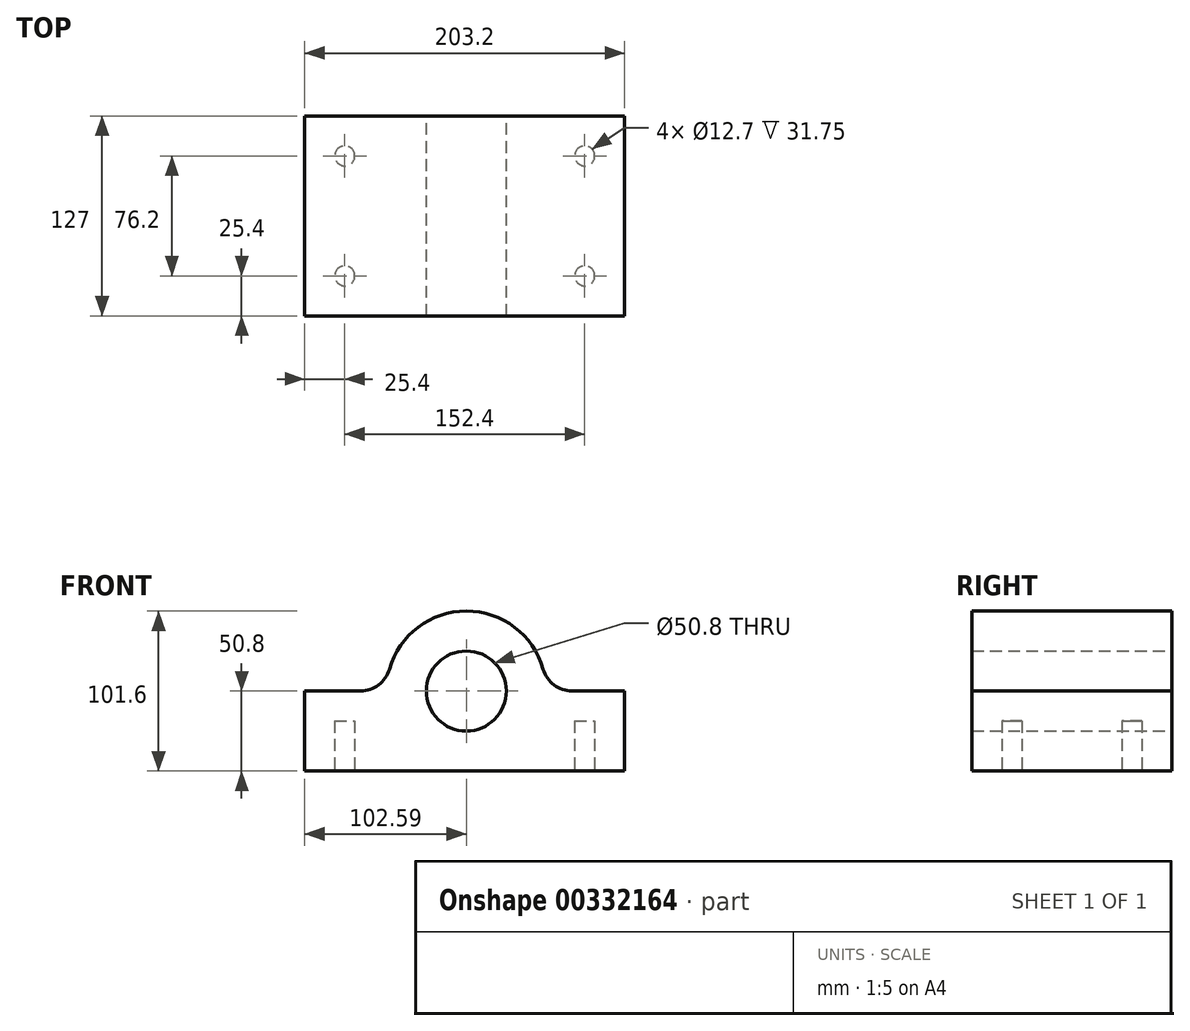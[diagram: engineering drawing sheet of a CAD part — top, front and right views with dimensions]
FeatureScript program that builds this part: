
annotation { "Feature Type Name" : "Feature", "Feature Type Description" : "" }
export const myFeature = defineFeature(function(context is Context, id is Id, definition is map)
    precondition{}
    {
        {
            var Q0;
            Q0=qCreatedBy(makeId("Front.planeOp"),FACE);
            var sketch = newSketch(context, id + "F0", { "sketchPlane" : qUnion([Q0])});
            skCircle(sketch, "E0", {"center": v(0, 0) * mm, "radius": 25.4 * mm});
            skLineSegment(sketch, "E1", {"start": v(100.6, 0) * mm, "end": v(100.6, -50.8) * mm});
            skLineSegment(sketch, "E2", {"start": v(100.6, -50.8) * mm, "end": v(-102.6, -50.8) * mm});
            skLineSegment(sketch, "E3", {"start": v(-102.6, -50.8) * mm, "end": v(-102.6, 0) * mm});
            skArc(sketch, "E4", {"start": v(48.87, 13.85) * mm, "mid": v(0, 50.8) * mm, "end": v(-48.87, 13.85) * mm});
            skLineSegment(sketch, "E5", {"start": v(-102.6, 0) * mm, "end": v(-67.2, 0) * mm});
            skLineSegment(sketch, "E6", {"start": v(100.6, 0) * mm, "end": v(67.2, 0) * mm});
            skArc(sketch, "E7", {"start": v(-67.2, 0) * mm, "mid": v(-55.71, 3.85) * mm, "end": v(-48.87, 13.85) * mm});
            skArc(sketch, "E8", {"start": v(48.87, 13.85) * mm, "mid": v(55.71, 3.85) * mm, "end": v(67.2, 0) * mm});
            skSolve(sketch);
        }
        {
            var Q0;
            Q0=makeQuery(id+"F0.imprint","IMPRINT",FACE,{"disambiguationData":[TD([[makeQuery(id+"F0.imprint","IMPRINT",EDGE,{"derivedFrom":sQuery(id+"F0.wireOp",EDGE,"E0")}),-1.0]])]});
            extrude(context, id + "F1", {"entities" : qUnion([Q0]), "depth" : 127 * mm});
        }
        {
            var Q0;
            Q0=makeQuery(id+"F1.opExtrude","SWEPT_FACE",FACE,{"disambiguationData":[OSD([sQuery(id+"F0.wireOp",EDGE,"E2")])]});
            var sketch = newSketch(context, id + "F2", { "sketchPlane" : qUnion([Q0])});
            skCircle(sketch, "E9", {"center": v(75.2, 101.6) * mm, "radius": 6.35 * mm});
            skCircle(sketch, "E10", {"center": v(75.2, 25.4) * mm, "radius": 6.35 * mm});
            skCircle(sketch, "E11", {"center": v(-77.2, 101.6) * mm, "radius": 6.35 * mm});
            skCircle(sketch, "E12", {"center": v(-77.2, 25.4) * mm, "radius": 6.35 * mm});
            skSolve(sketch);
        }
        {
            var Q0;
            Q0=makeQuery(id+"F2.imprint","IMPRINT",FACE,{"disambiguationData":[TD([[makeQuery(id+"F2.imprint","IMPRINT",EDGE,{"derivedFrom":sQuery(id+"F2.wireOp",EDGE,"E11")}),1.0]])]});
            var Q1;
            Q1=makeQuery(id+"F2.imprint","IMPRINT",FACE,{"disambiguationData":[TD([[makeQuery(id+"F2.imprint","IMPRINT",EDGE,{"derivedFrom":sQuery(id+"F2.wireOp",EDGE,"E9")}),1.0]])]});
            var Q2;
            Q2=makeQuery(id+"F2.imprint","IMPRINT",FACE,{"disambiguationData":[TD([[makeQuery(id+"F2.imprint","IMPRINT",EDGE,{"derivedFrom":sQuery(id+"F2.wireOp",EDGE,"E10")}),1.0]])]});
            var Q3;
            Q3=makeQuery(id+"F2.imprint","IMPRINT",FACE,{"disambiguationData":[TD([[makeQuery(id+"F2.imprint","IMPRINT",EDGE,{"derivedFrom":sQuery(id+"F2.wireOp",EDGE,"E12")}),1.0]])]});
            extrude(context, id + "F3", {"entities" : qUnion([Q0, Q1, Q2, Q3]), "operationType" : NewBodyOperationType.REMOVE, "oppositeDirection" : true, "depth" : 31.75 * mm});
        }
    });
